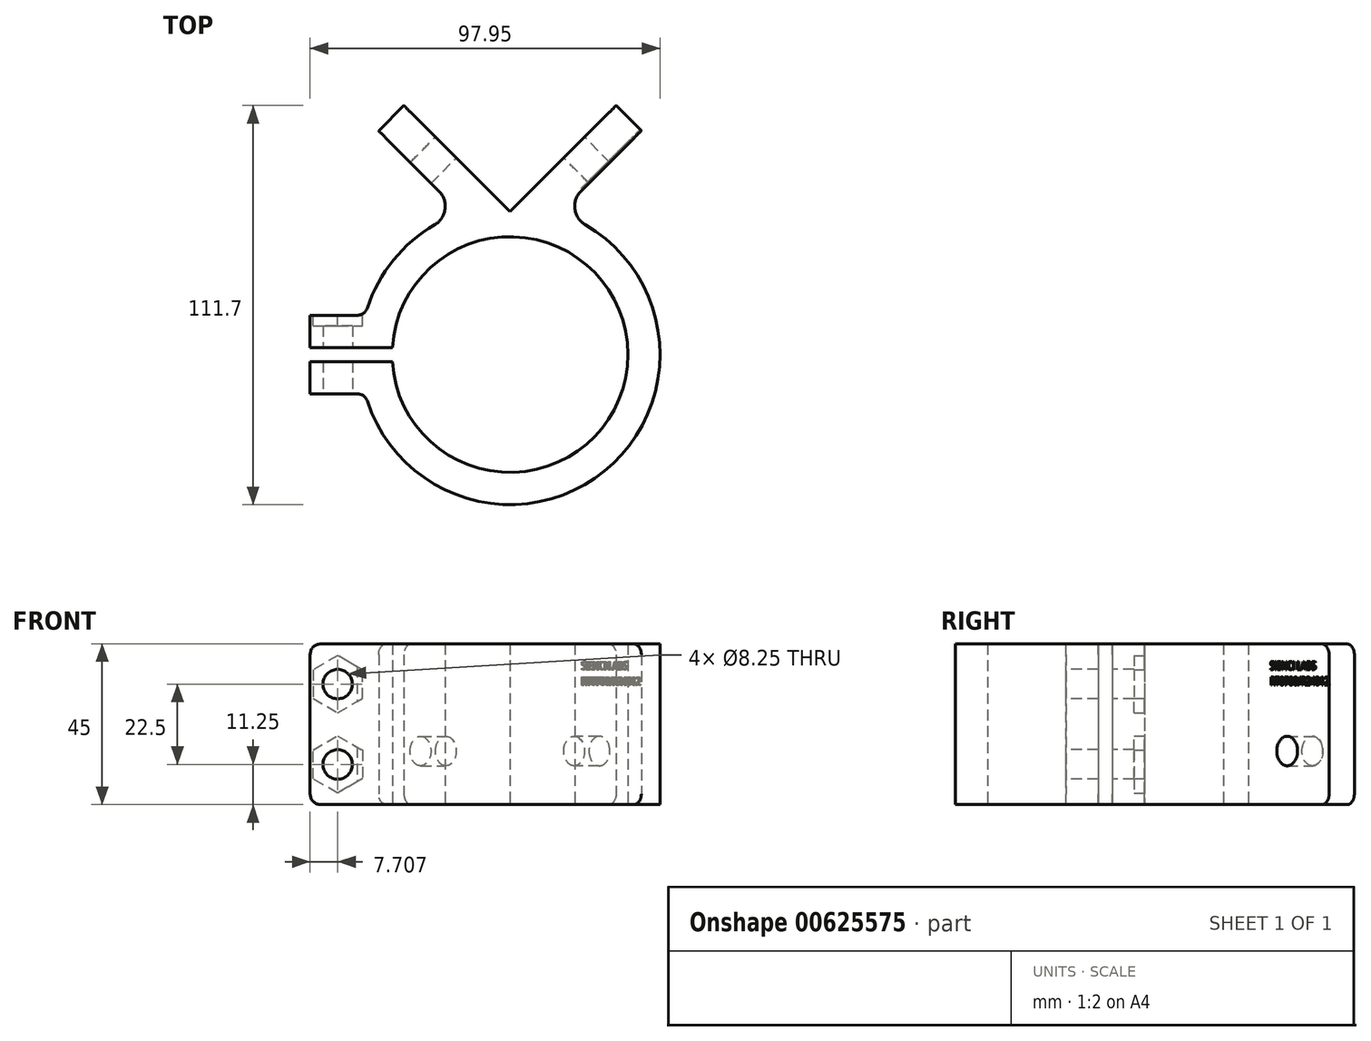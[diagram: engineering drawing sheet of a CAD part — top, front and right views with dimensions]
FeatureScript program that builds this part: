
annotation { "Feature Type Name" : "Feature", "Feature Type Description" : "" }
export const myFeature = defineFeature(function(context is Context, id is Id, definition is map)
    precondition{}
    {
        {
            var Q0;
            Q0=qCreatedBy(makeId("Top.planeOp"),FACE);
            var sketch = newSketch(context, id + "F0", { "sketchPlane" : qUnion([Q0])});
            skLineSegment(sketch, "E0", {"start": v(0, 0) * mm, "end": v(-29.7, 29.7) * mm});
            skLineSegment(sketch, "E1", {"start": v(0, 38.94) * mm, "end": v(0, 0) * mm, "construction": true});
            skLineSegment(sketch, "E2", {"start": v(-29.7, 29.7) * mm, "end": v(-36.77, 22.63) * mm});
            skLineSegment(sketch, "E3", {"start": v(-36.77, 22.63) * mm, "end": v(-13.8, -0.33) * mm});
            skLineSegment(sketch, "E4", {"start": v(0, 0) * mm, "end": v(0, -40) * mm, "construction": true});
            skArc(sketch, "E5", {"start": v(-32.94, -42) * mm, "mid": v(33, -40) * mm, "end": v(-32.94, -38) * mm});
            skArc(sketch, "E6", {"start": v(-41.95, -42) * mm, "mid": v(25.14, -73.64) * mm, "end": v(13.8, -0.33) * mm});
            skLineSegment(sketch, "E7", {"start": v(0, -40) * mm, "end": v(-42, -40) * mm, "construction": true});
            skLineSegment(sketch, "E8", {"start": v(-41.95, -38) * mm, "end": v(-55.95, -38) * mm});
            skLineSegment(sketch, "E9", {"start": v(-55.95, -38) * mm, "end": v(-55.95, -29) * mm});
            skLineSegment(sketch, "E10", {"start": v(-55.95, -29) * mm, "end": v(-40.53, -29) * mm});
            skLineSegment(sketch, "E11.MirrorCS", {"start": v(-55.95, -42) * mm, "end": v(-55.95, -51) * mm});
            skLineSegment(sketch, "E12.MirrorCS", {"start": v(-55.95, -51) * mm, "end": v(-40.53, -51) * mm});
            skLineSegment(sketch, "E13.MirrorCS", {"start": v(-41.95, -42) * mm, "end": v(-55.95, -42) * mm});
            skLineSegment(sketch, "E14", {"start": v(-41.95, -38) * mm, "end": v(-32.94, -38) * mm});
            skLineSegment(sketch, "E15.MirrorCS", {"start": v(-41.95, -42) * mm, "end": v(-32.94, -42) * mm});
            skLineSegment(sketch, "E16.MirrorCS", {"start": v(29.7, 29.7) * mm, "end": v(36.77, 22.63) * mm});
            skLineSegment(sketch, "E17.MirrorCS", {"start": v(0, 0) * mm, "end": v(29.7, 29.7) * mm});
            skLineSegment(sketch, "E18.MirrorCS", {"start": v(36.77, 22.63) * mm, "end": v(13.8, -0.33) * mm});
            skPoint(sketch, "E19.orphan", {"position": v(0, -14.14) * mm});
            skArc(sketch, "E20.trimOffspring", {"start": v(-13.8, -0.33) * mm, "mid": v(-33.64, -14.86) * mm, "end": v(-41.95, -38) * mm});
            skSolve(sketch);
        }
        {
            var Q0;
            Q0=makeQuery(id+"F0.imprint","IMPRINT",FACE,{"disambiguationData":[TD([[makeQuery(id+"F0.imprint","IMPRINT",EDGE,{"derivedFrom":sQuery(id+"F0.wireOp",EDGE,"E0")}),1.0]])]});
            var Q1;
            {var subQ4=sQuery(id+"F0.wireOp",EDGE,"E9");Q1=makeQuery(id+"F0.imprint","IMPRINT",FACE,{"disambiguationData":[TD([[makeQuery(id+"F0.imprint","IMPRINT",EDGE,{"derivedFrom":subQ4}),-1.0]])]});}
            var Q2;
            {var subQ1=sQuery(id+"F0.wireOp",EDGE,"E11.MirrorCS");Q2=makeQuery(id+"F0.imprint","IMPRINT",FACE,{"disambiguationData":[TD([[makeQuery(id+"F0.imprint","IMPRINT",EDGE,{"derivedFrom":subQ1}),1.0]])]});}
            extrude(context, id + "F1", {"entities" : qUnion([Q0, Q1, Q2]), "depth" : 45 * mm, "offsetDistance" : 25 * mm});
        }
        {
            var Q0;
            Q0=makeQuery(id+"F1.opExtrude","SWEPT_FACE",FACE,{"disambiguationData":[OSD([sQuery(id+"F0.wireOp",EDGE,"E17.MirrorCS")])]});
            var sketch = newSketch(context, id + "F2", { "sketchPlane" : qUnion([Q0])});
            skLineSegment(sketch, "E21", {"start": v(0, 15) * mm, "end": v(-50.8, 15) * mm, "construction": true});
            skCircle(sketch, "E22", {"center": v(-25.4, 15) * mm, "radius": 4.12 * mm});
            skSolve(sketch);
        }
        {
            var Q0;
            Q0=qSketchRegion(id+"F2",true);
            extrude(context, id + "F3", {"entities" : qUnion([Q0]), "operationType" : NewBodyOperationType.REMOVE, "endBound" : BoundingType.UP_TO_NEXT, "oppositeDirection" : true, "depth" : 25 * mm, "offsetDistance" : 25 * mm});
        }
        {
            var Q0;
            Q0=makeQuery(id+"F1.opExtrude","SWEPT_FACE",FACE,{"disambiguationData":[OSD([sQuery(id+"F0.wireOp",EDGE,"E0")])]});
            var sketch = newSketch(context, id + "F4", { "sketchPlane" : qUnion([Q0])});
            skLineSegment(sketch, "E23", {"start": v(0, 15) * mm, "end": v(50.8, 15) * mm, "construction": true});
            skCircle(sketch, "E24", {"center": v(25.4, 15) * mm, "radius": 4.12 * mm});
            skSolve(sketch);
        }
        {
            var Q0;
            Q0=qSketchRegion(id+"F4",true);
            extrude(context, id + "F5", {"entities" : qUnion([Q0]), "operationType" : NewBodyOperationType.REMOVE, "endBound" : BoundingType.UP_TO_NEXT, "oppositeDirection" : true, "depth" : 25 * mm, "offsetDistance" : 25 * mm});
        }
        {
            var Q0;
            Q0=makeQuery(id+"F1.opExtrude","SWEPT_FACE",FACE,{"disambiguationData":[OSD([sQuery(id+"F0.wireOp",EDGE,"E12.MirrorCS")])]});
            var sketch = newSketch(context, id + "F6", { "sketchPlane" : qUnion([Q0])});
            skLineSegment(sketch, "E25", {"start": v(-48.24, 45) * mm, "end": v(-48.24, 0) * mm, "construction": true});
            skLineSegment(sketch, "E26", {"start": v(-55.95, 22.5) * mm, "end": v(-40.53, 22.5) * mm, "construction": true});
            skLineSegment(sketch, "E27", {"start": v(-55.95, 22.5) * mm, "end": v(-40.53, 45) * mm, "construction": true});
            skCircle(sketch, "E28", {"center": v(-48.24, 33.75) * mm, "radius": 4.12 * mm});
            skCircle(sketch, "E29.MirrorC", {"center": v(-48.24, 11.25) * mm, "radius": 4.12 * mm});
            skLineSegment(sketch, "E30.MirrorCS", {"start": v(-55.95, 22.5) * mm, "end": v(-40.53, 0) * mm, "construction": true});
            skSolve(sketch);
        }
        {
            var Q0;
            Q0=qSketchRegion(id+"F6",true);
            var Q1;
            Q1=makeQuery(id+"F1.opExtrude","SWEPT_FACE",FACE,{"disambiguationData":[OSD([sQuery(id+"F0.wireOp",EDGE,"E10")])]});
            extrude(context, id + "F7", {"entities" : qUnion([Q0]), "operationType" : NewBodyOperationType.REMOVE, "endBound" : BoundingType.UP_TO_SURFACE, "oppositeDirection" : true, "depth" : 25 * mm, "endBoundEntityFace" : qUnion([Q1]), "offsetDistance" : 25 * mm});
        }
        {
            var Q0;
            Q0=makeQuery(id+"F1.opExtrude","CAP_EDGE",EDGE,{"disambiguationData":[OSD([sQuery(id+"F0.wireOp",EDGE,"E9")])],"isStart":false});
            var Q1;
            Q1=makeQuery(id+"F1.opExtrude","CAP_EDGE",EDGE,{"disambiguationData":[OSD([sQuery(id+"F0.wireOp",EDGE,"E11.MirrorCS")])],"isStart":false});
            var Q2;
            Q2=makeQuery(id+"F1.opExtrude","CAP_EDGE",EDGE,{"disambiguationData":[OSD([sQuery(id+"F0.wireOp",EDGE,"E11.MirrorCS")])],"isStart":true});
            var Q3;
            Q3=makeQuery(id+"F1.opExtrude","CAP_EDGE",EDGE,{"disambiguationData":[OSD([sQuery(id+"F0.wireOp",EDGE,"E9")])],"isStart":true});
            var Q4;
            Q4=makeQuery(id+"F1.opExtrude","CAP_EDGE",EDGE,{"disambiguationData":[OSD([sQuery(id+"F0.wireOp",EDGE,"E2")])],"isStart":false});
            var Q5;
            Q5=makeQuery(id+"F1.opExtrude","CAP_EDGE",EDGE,{"disambiguationData":[OSD([sQuery(id+"F0.wireOp",EDGE,"E16.MirrorCS")])],"isStart":false});
            var Q6;
            Q6=makeQuery(id+"F1.opExtrude","CAP_EDGE",EDGE,{"disambiguationData":[OSD([sQuery(id+"F0.wireOp",EDGE,"E16.MirrorCS")])],"isStart":true});
            var Q7;
            Q7=makeQuery(id+"F1.opExtrude","CAP_EDGE",EDGE,{"disambiguationData":[OSD([sQuery(id+"F0.wireOp",EDGE,"E2")])],"isStart":true});
            var Q8;
            Q8=makeQuery(id+"F1.opExtrude","SWEPT_EDGE",EDGE,{"disambiguationData":[OSD([sQuery(id+"F0.wireOp",EDGE,"E10"),sQuery(id+"F0.wireOp",EDGE,"E20.trimOffspring")])]});
            var Q9;
            Q9=makeQuery(id+"F1.opExtrude","SWEPT_EDGE",EDGE,{"disambiguationData":[OSD([sQuery(id+"F0.wireOp",EDGE,"E6"),sQuery(id+"F0.wireOp",EDGE,"E12.MirrorCS")])]});
            fillet(context, id + "F8", {"entities" : qUnion([Q0, Q1, Q2, Q3, Q4, Q5, Q6, Q7, Q8, Q9]), "radius" : 3 * mm, "tangentPropagation" : true, "allowEdgeOverflow" : false});
        }
        {
            var Q0;
            Q0=makeQuery(id+"F1.opExtrude","SWEPT_FACE",FACE,{"disambiguationData":[OSD([sQuery(id+"F0.wireOp",EDGE,"E10")])]});
            var sketch = newSketch(context, id + "F9", { "sketchPlane" : qUnion([Q0])});
            skCircle(sketch, "E31.cCircle", {"center": v(48.24, 33.75) * mm, "radius": 6.92 * mm, "construction": true});
            skLineSegment(sketch, "E31.0", {"start": v(48.24, 41.75) * mm, "end": v(55.17, 37.75) * mm});
            skLineSegment(sketch, "E31.1", {"start": v(55.17, 37.75) * mm, "end": v(55.17, 29.75) * mm});
            skLineSegment(sketch, "E31.2", {"start": v(55.17, 29.75) * mm, "end": v(48.24, 25.75) * mm});
            skLineSegment(sketch, "E31.3", {"start": v(48.24, 25.75) * mm, "end": v(41.32, 29.75) * mm});
            skLineSegment(sketch, "E31.4", {"start": v(41.32, 29.75) * mm, "end": v(41.32, 37.75) * mm});
            skLineSegment(sketch, "E31.5", {"start": v(41.32, 37.75) * mm, "end": v(48.24, 41.75) * mm});
            skPoint(sketch, "E31.0.midPoint", {"position": v(51.7, 39.75) * mm});
            skLineSegment(sketch, "E32", {"start": v(74.38, 22.5) * mm, "end": v(55.95, 22.5) * mm, "construction": true});
            skLineSegment(sketch, "E33.MirrorCS", {"start": v(55.17, 15.25) * mm, "end": v(48.24, 19.25) * mm});
            skLineSegment(sketch, "E34.MirrorCS", {"start": v(41.32, 15.25) * mm, "end": v(41.32, 7.25) * mm});
            skLineSegment(sketch, "E35.MirrorCS", {"start": v(48.24, 3.25) * mm, "end": v(55.17, 7.25) * mm});
            skLineSegment(sketch, "E36.MirrorCS", {"start": v(48.24, 19.25) * mm, "end": v(41.32, 15.25) * mm});
            skCircle(sketch, "E37.MirrorC", {"center": v(48.24, 11.25) * mm, "radius": 6.92 * mm, "construction": true});
            skLineSegment(sketch, "E38.MirrorCS", {"start": v(55.17, 7.25) * mm, "end": v(55.17, 15.25) * mm});
            skLineSegment(sketch, "E39.MirrorCS", {"start": v(41.32, 7.25) * mm, "end": v(48.24, 3.25) * mm});
            skPoint(sketch, "E40.MirrorP", {"position": v(51.7, 5.25) * mm});
            skSolve(sketch);
        }
        {
            var Q0;
            Q0=qSketchRegion(id+"F9",true);
            extrude(context, id + "F10", {"entities" : qUnion([Q0]), "operationType" : NewBodyOperationType.REMOVE, "oppositeDirection" : true, "depth" : 3 * mm, "offsetDistance" : 25 * mm});
        }
        {
            var Q0;
            Q0=makeQuery(id+"F1.opExtrude","SWEPT_EDGE",EDGE,{"disambiguationData":[OSD([sQuery(id+"F0.wireOp",EDGE,"E3"),sQuery(id+"F0.wireOp",EDGE,"E20.trimOffspring")])]});
            var Q1;
            Q1=makeQuery(id+"F1.opExtrude","SWEPT_EDGE",EDGE,{"disambiguationData":[OSD([sQuery(id+"F0.wireOp",EDGE,"E6"),sQuery(id+"F0.wireOp",EDGE,"E18.MirrorCS")])]});
            fillet(context, id + "F11", {"entities" : qUnion([Q0, Q1]), "radius" : 6 * mm, "tangentPropagation" : true, "allowEdgeOverflow" : false});
        }
        {
            var Q0;
            Q0=makeQuery(id+"F1.opExtrude","SWEPT_FACE",FACE,{"disambiguationData":[OSD([sQuery(id+"F0.wireOp",EDGE,"E18.MirrorCS")])]});
            var sketch = newSketch(context, id + "F12", { "sketchPlane" : qUnion([Q0])});
            skText(sketch, "E41", { "text": "SIENCI LABS\nRT0700/R24012", "fontName": "OpenSans-Regular.ttf"});
            const initialGuessF12  = {"E41": [0.01863, 0.0378, 1, 0, 0.0023]};
            skSetInitialGuess(sketch, initialGuessF12);
            skSolve(sketch);
        }
        {
            var Q0;
            Q0=qSketchRegion(id+"F12",true);
            extrude(context, id + "F13", {"entities" : qUnion([Q0]), "operationType" : NewBodyOperationType.REMOVE, "oppositeDirection" : true, "depth" : 0.5 * mm, "offsetDistance" : 25 * mm});
        }
    });
